# Revit family: 32L 2 to 6 units single sided outdoor manifold system REVISED
name_source: partatom
category: Plumbing Fixtures
revit_build: Autodesk Revit LT 2016 (Build: 20150220_1215(x64)
units: mm (PartAtom-declared; Revit-internal decimal feet)

## family parameters
Always vertical = Yes
Cut with Voids When Loaded = No
Part Type = Normal
Room Calculation Point = No
Round Connector Dimension = Use Diameter
Shared = No
Work Plane-Based = No

## types (10) — shared parameters
Cold Water Inlet Pipe connector description = Male threaded connector R1-1/2"
Cold Water Inlet Pipe diameter = 38.1mm(DN 40)
Gas Inlet Pipe connector description = Male threaded connector R1-1/2"
Gas Inlet Pipe diameter = 38.1mm(DN 40)
Hot Water Outlet Pipe connector description = Male threaded connector R1-1/2"
Hot Water Outlet Pipe diameter = 38.1mm(DN 40)

## per-type parameters (varying)
| type | 2 Unit L | 2 Unit R | 3 Unit L | 3 Unit R | Base Offset L | Base Offset R | Base Support L | Base Support R | Connector Left | Connector Right | No. of power supply point required | Nominal depth | Nominal height | Nominal width | Number of Gas Water Heaters | Product SKU Dux brand | Product SKU Thermann brand | Product description | Total Max. power requirement | Total nominal gas consumption (MJ/h) | Weight (Kg) |
| 32L 2 units single sided outdoor floor mounted | Yes | No | No | No | 1040 mm | 1040 mm | Yes | No | 1030 mm | 0 mm | 2 | 900mm | 1540mm | 1040mm | 2 | D23200EN/LFx | T23200EN/LFx | Gas Water heater Manifold 2 unit outdoor floor mounted | 446W | 434 | 110 |
| 32L 3 units single sided outdoor floor mounted | No | No | Yes | No | 1540 mm | 1040 mm | Yes | No | 1530 mm | 0 mm | 3 | 900mm | 1540mm | 1540mm | 3 | D33200EN/LFx | T33200EN/LFx | Gas Water heater Manifold 3 unit outdoor floor mounted | 669W | 651 | 140 |
| 32L 4 units single sided outdoor floor mounted | Yes | Yes | No | No | 1040 mm | 1040 mm | Yes | Yes | 1030 mm | 1040 mm | 4 | 900mm | 1540mm | 2080mm | 4 | D43200EN/LFx | T43200EN/LFx | Gas Water heater Manifold 4 unit outdoor floor mounted | 892W | 868 | 220 |
| 32L 5 units single sided outdoor floor mounted | No | Yes | Yes | No | 1540 mm | 1040 mm | Yes | Yes | 1530 mm | 1040 mm | 5 | 900mm | 1540mm | 2580mm | 5 | D53200EN/LFx | T53200EN/LFx | Gas Water heater Manifold 5 unit outdoor floor mounted | 1115W | 1085 | 250 |
| 32L 6 units single sided outdoor floor mounted | No | No | Yes | Yes | 1540 mm | 1540 mm | Yes | Yes | 1530 mm | 1540 mm | 6 | 900mm | 1540mm | 3080mm | 6 | D63200EN/LFx | T63200EN/LFx | Gas Water heater Manifold 6 unit  outdoor floor mounted | 1338W | 1302 | 280 |
| 32L 2 units single sided outdoor wall mounted | Yes | No | No | No | 1040 mm | 1040 mm | No | No | 1030 mm | 0 mm | 2 | 310mm | 1500mm | 1040mm | 2 | D23200EN/LWx | T23200EN/LWx | Gas Water heater Manifold 2 unit outdoor wall mounted | 446W | 434 | 110 |
| 32L 3 units single sided outdoor wall mounted | No | No | Yes | No | 1540 mm | 1040 mm | No | No | 1530 mm | 0 mm | 3 | 310mm | 1500mm | 1540mm | 3 | D33200EN/LWx | T33200EN/LWx | Gas Water heater Manifold 3 unit outdoor wall mounted | 669W | 651 | 140 |
| 32L 4 units single sided outdoor wall mounted | Yes | Yes | No | No | 1040 mm | 1040 mm | No | No | 1030 mm | 1040 mm | 4 | 310mm | 1500mm | 2080mm | 4 | D43200EN/LWx | T43200EN/LWx | Gas Water heater Manifold 4 unit outdoor wall mounted | 892W | 868 | 220 |
| 32L 5 units single sided outdoor wall mounted | No | Yes | Yes | No | 1540 mm | 1040 mm | No | No | 1530 mm | 1040 mm | 5 | 310mm | 1500mm | 2580mm | 5 | D53200EN/LWx | T53200EN/LWx | Gas Water heater Manifold 5 unit  outdoor wall mounted | 1115W | 1085 | 250 |
| 32L 6 units single sided outdoor wall mounted | No | No | Yes | Yes | 1040 mm | 1040 mm | No | No | 1530 mm | 1540 mm | 6 | 310mm | 1500mm | 3080mm | 6 | D63200EN/LWx | T63200EN/LWx | Gas Water heater Manifold 6 unit outdoor wall mounted | 1338W | 1302 | 280 |

## geometry (parser evidence)
native form markers: Sweep x16
no freeform markers — native parametric forms only
